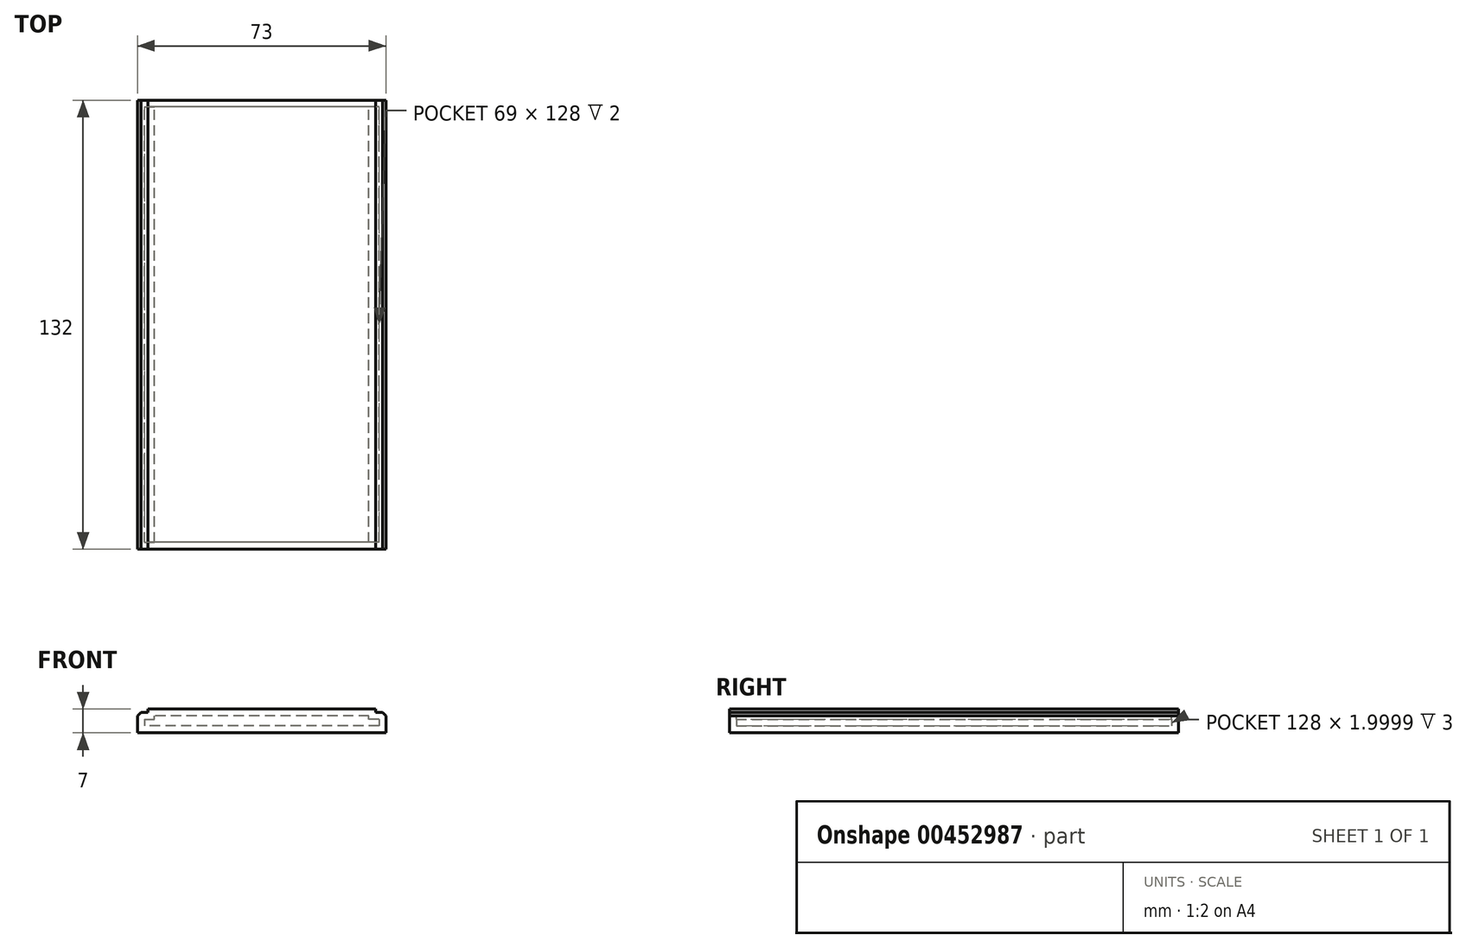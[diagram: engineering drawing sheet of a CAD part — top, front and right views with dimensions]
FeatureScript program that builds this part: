
annotation { "Feature Type Name" : "Feature", "Feature Type Description" : "" }
export const myFeature = defineFeature(function(context is Context, id is Id, definition is map)
    precondition{}
    {
        {
            var Q0;
            Q0=qCreatedBy(makeId("Front.planeOp"),FACE);
            var sketch = newSketch(context, id + "F0", { "sketchPlane" : qUnion([Q0])});
            skLineSegment(sketch, "E0", {"start": v(27.16, -5.1) * mm, "end": v(30.16, -5.1) * mm});
            skLineSegment(sketch, "E1.bottom", {"start": v(-39.84, -5.1) * mm, "end": v(-42.84, -5.1) * mm});
            skLineSegment(sketch, "E2.left", {"start": v(27.16, 0.9) * mm, "end": v(27.16, 0.9) * mm});
            skLineSegment(sketch, "E3.bottom", {"start": v(29.16, 0.9) * mm, "end": v(27.16, 0.9) * mm});
            skLineSegment(sketch, "E4", {"start": v(-42.84, -0.1) * mm, "end": v(-41.84, 0.9) * mm});
            skLineSegment(sketch, "E5", {"start": v(30.16, -0.1) * mm, "end": v(29.16, 0.9) * mm});
            skLineSegment(sketch, "E6", {"start": v(-42.84, -0.1) * mm, "end": v(-42.84, -5.1) * mm});
            skLineSegment(sketch, "E7", {"start": v(-41.84, 0.9) * mm, "end": v(-39.84, 0.9) * mm});
            skLineSegment(sketch, "E8", {"start": v(-39.84, 0.9) * mm, "end": v(-39.84, 1.9) * mm});
            skLineSegment(sketch, "E9", {"start": v(30.16, -0.1) * mm, "end": v(30.16, -5.1) * mm});
            skLineSegment(sketch, "E10", {"start": v(27.16, 0.9) * mm, "end": v(27.16, 1.9) * mm});
            skLineSegment(sketch, "E11", {"start": v(27.16, 1.9) * mm, "end": v(-39.84, 1.9) * mm});
            skLineSegment(sketch, "E12", {"start": v(-39.84, -5.1) * mm, "end": v(27.16, -5.1) * mm});
            skSolve(sketch);
        }
        {
            var Q0;
            Q0 = qSketchRegion(id + "F0", true);
            extrude(context, id + "F1", {"entities" : qUnion([Q0]), "depth" : 132 * mm});
        }
        {
            var Q0;
            Q0=makeQuery(id+"F1.opExtrude","SWEPT_BODY",BODY,{"disambiguationData":[OSD([sQuery(id+"F0.wireOp",EDGE,"E0"),sQuery(id+"F0.wireOp",EDGE,"E1.bottom"),sQuery(id+"F0.wireOp",EDGE,"E3.bottom"),sQuery(id+"F0.wireOp",EDGE,"E4"),sQuery(id+"F0.wireOp",EDGE,"E5"),sQuery(id+"F0.wireOp",EDGE,"E6"),sQuery(id+"F0.wireOp",EDGE,"E7"),sQuery(id+"F0.wireOp",EDGE,"E8"),sQuery(id+"F0.wireOp",EDGE,"E9"),sQuery(id+"F0.wireOp",EDGE,"E10"),sQuery(id+"F0.wireOp",EDGE,"E11"),sQuery(id+"F0.wireOp",EDGE,"E12")])]});
            var Q1;
            Q1=qCreatedBy(makeId("Top.planeOp"),FACE);
            transform(context, id + "F2", {"entities" : qUnion([Q0]), "transformType" : TransformType.TRANSLATION_DISTANCE, "transformDirection" : qUnion([Q1]), "distance" : 8 * mm, "makeCopy" : false});
        }
        {
            var Q0;
            Q0=makeQuery(id+"F1.opExtrude","SWEPT_BODY",BODY,{"disambiguationData":[OSD([sQuery(id+"F0.wireOp",EDGE,"E0"),sQuery(id+"F0.wireOp",EDGE,"E1.bottom"),sQuery(id+"F0.wireOp",EDGE,"E3.bottom"),sQuery(id+"F0.wireOp",EDGE,"E4"),sQuery(id+"F0.wireOp",EDGE,"E5"),sQuery(id+"F0.wireOp",EDGE,"E6"),sQuery(id+"F0.wireOp",EDGE,"E7"),sQuery(id+"F0.wireOp",EDGE,"E8"),sQuery(id+"F0.wireOp",EDGE,"E9"),sQuery(id+"F0.wireOp",EDGE,"E10"),sQuery(id+"F0.wireOp",EDGE,"E11"),sQuery(id+"F0.wireOp",EDGE,"E12")])]});
            var Q1;
            Q1=qCreatedBy(makeId("Front.planeOp"),FACE);
            transform(context, id + "F3", {"entities" : qUnion([Q0]), "transformType" : TransformType.TRANSLATION_DISTANCE, "transformDirection" : qUnion([Q1]), "distance" : 70 * mm, "oppositeDirection" : true, "makeCopy" : false});
        }
        {
            var Q0;
            Q0=makeQuery(id+"F1.opExtrude","CAP_FACE",FACE,{"disambiguationData":[OSD([sQuery(id+"F0.wireOp",EDGE,"E0"),sQuery(id+"F0.wireOp",EDGE,"E1.bottom"),sQuery(id+"F0.wireOp",EDGE,"E3.bottom"),sQuery(id+"F0.wireOp",EDGE,"E4"),sQuery(id+"F0.wireOp",EDGE,"E5"),sQuery(id+"F0.wireOp",EDGE,"E6"),sQuery(id+"F0.wireOp",EDGE,"E7"),sQuery(id+"F0.wireOp",EDGE,"E8"),sQuery(id+"F0.wireOp",EDGE,"E9"),sQuery(id+"F0.wireOp",EDGE,"E10"),sQuery(id+"F0.wireOp",EDGE,"E11"),sQuery(id+"F0.wireOp",EDGE,"E12")])],"isStart":false});
            var Q1;
            Q1=makeQuery(id+"F1.opExtrude","SWEPT_BODY",BODY,{"disambiguationData":[OSD([sQuery(id+"F0.wireOp",EDGE,"E0"),sQuery(id+"F0.wireOp",EDGE,"E1.bottom"),sQuery(id+"F0.wireOp",EDGE,"E3.bottom"),sQuery(id+"F0.wireOp",EDGE,"E4"),sQuery(id+"F0.wireOp",EDGE,"E5"),sQuery(id+"F0.wireOp",EDGE,"E6"),sQuery(id+"F0.wireOp",EDGE,"E7"),sQuery(id+"F0.wireOp",EDGE,"E8"),sQuery(id+"F0.wireOp",EDGE,"E9"),sQuery(id+"F0.wireOp",EDGE,"E10"),sQuery(id+"F0.wireOp",EDGE,"E11"),sQuery(id+"F0.wireOp",EDGE,"E12")])]});
            shell(context, id + "F4", {"isHollow" : true, "entities" : qUnion([Q0]), "parts" : qUnion([Q1]), "thickness" : 2 * mm});
        }
    });
